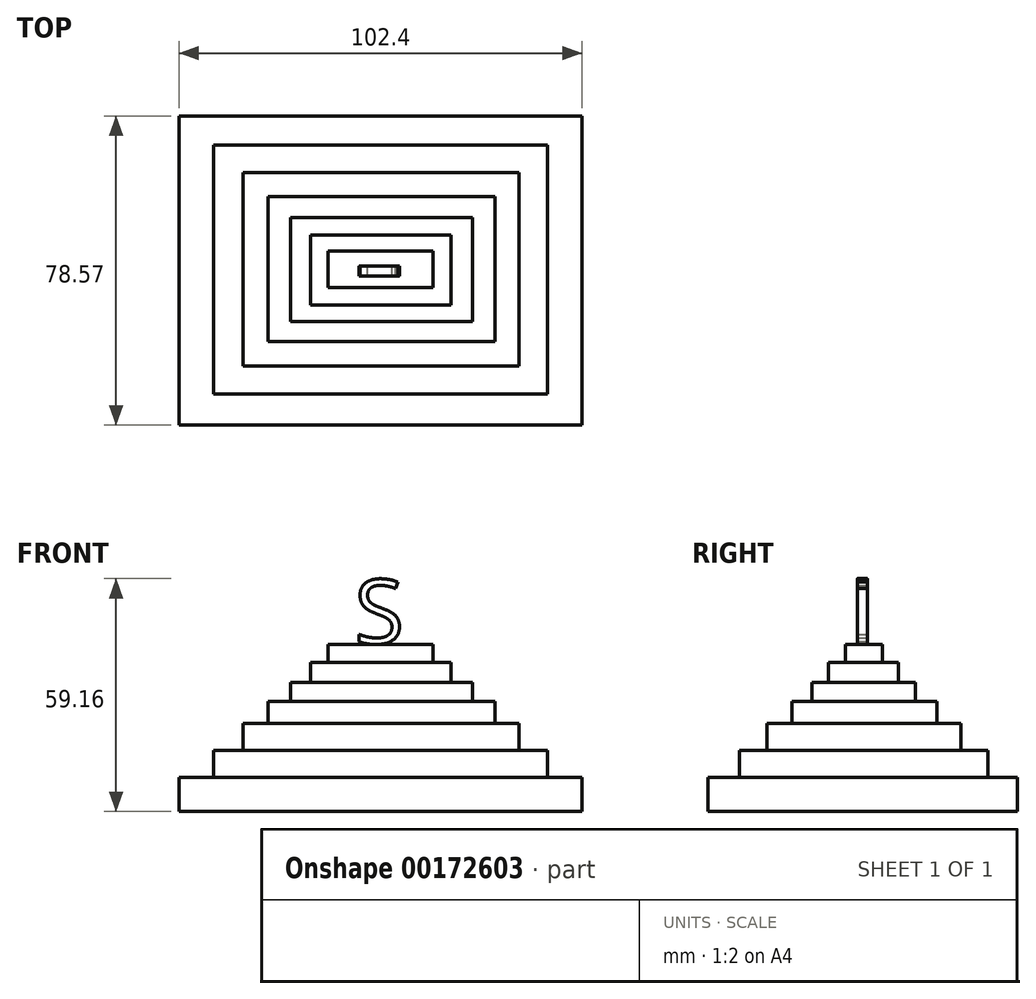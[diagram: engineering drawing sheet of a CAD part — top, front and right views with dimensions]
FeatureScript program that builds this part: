
annotation { "Feature Type Name" : "Feature", "Feature Type Description" : "" }
export const myFeature = defineFeature(function(context is Context, id is Id, definition is map)
    precondition{}
    {
        {
            var Q0;
            Q0=qCreatedBy(makeId("Top.planeOp"),FACE);
            var sketch = newSketch(context, id + "F0", { "sketchPlane" : qUnion([Q0])});
            skLineSegment(sketch, "E0.bottom", {"start": v(-50.86, 38.1) * mm, "end": v(51.54, 38.1) * mm});
            skLineSegment(sketch, "E0.top", {"start": v(-50.86, -40.47) * mm, "end": v(51.54, -40.47) * mm});
            skLineSegment(sketch, "E0.left", {"start": v(-50.86, 38.1) * mm, "end": v(-50.86, -40.47) * mm});
            skLineSegment(sketch, "E0.right", {"start": v(51.54, 38.1) * mm, "end": v(51.54, -40.47) * mm});
            skSolve(sketch);
        }
        {
            var Q0;
            Q0=qSketchRegion(id+"F0",true);
            var Q1;
            Q1=qSketchRegion(id+"FIFzSHws54il2H1_1",true);
            extrude(context, id + "F1", {"entities" : qUnion([Q0, Q1]), "depth" : 8.64 * mm});
        }
        {
            var Q0;
            Q0=qCreatedBy(makeId("Top.planeOp"),FACE);
            var sketch = newSketch(context, id + "F2", { "sketchPlane" : qUnion([Q0])});
            skLineSegment(sketch, "E1.bottom", {"start": v(-42.07, 30.67) * mm, "end": v(42.75, 30.67) * mm});
            skLineSegment(sketch, "E1.top", {"start": v(-42.07, -32.53) * mm, "end": v(42.75, -32.53) * mm});
            skLineSegment(sketch, "E1.left", {"start": v(-42.07, 30.67) * mm, "end": v(-42.07, -32.53) * mm});
            skLineSegment(sketch, "E1.right", {"start": v(42.75, 30.67) * mm, "end": v(42.75, -32.53) * mm});
            skSolve(sketch);
        }
        {
            var Q0;
            Q0=qSketchRegion(id+"F2",true);
            extrude(context, id + "F3", {"entities" : qUnion([Q0]), "operationType" : NewBodyOperationType.ADD, "depth" : 15.5 * mm});
        }
        {
            var Q0;
            Q0=qCreatedBy(makeId("Top.planeOp"),FACE);
            var sketch = newSketch(context, id + "F4", { "sketchPlane" : qUnion([Q0])});
            skLineSegment(sketch, "E2.bottom", {"start": v(-34.64, 23.74) * mm, "end": v(35.48, 23.74) * mm});
            skLineSegment(sketch, "E2.top", {"start": v(-34.64, -25.43) * mm, "end": v(35.48, -25.43) * mm});
            skLineSegment(sketch, "E2.left", {"start": v(-34.64, 23.74) * mm, "end": v(-34.64, -25.43) * mm});
            skLineSegment(sketch, "E2.right", {"start": v(35.48, 23.74) * mm, "end": v(35.48, -25.43) * mm});
            skSolve(sketch);
        }
        {
            var Q0;
            Q0=qSketchRegion(id+"F4",true);
            extrude(context, id + "F5", {"entities" : qUnion([Q0]), "operationType" : NewBodyOperationType.ADD, "depth" : 22.35 * mm});
        }
        {
            var Q0;
            Q0=qCreatedBy(makeId("Top.planeOp"),FACE);
            var sketch = newSketch(context, id + "F6", { "sketchPlane" : qUnion([Q0])});
            skLineSegment(sketch, "E3.bottom", {"start": v(-28.22, 17.66) * mm, "end": v(29.4, 17.66) * mm});
            skLineSegment(sketch, "E3.top", {"start": v(-28.22, -19.18) * mm, "end": v(29.4, -19.18) * mm});
            skLineSegment(sketch, "E3.left", {"start": v(-28.22, 17.66) * mm, "end": v(-28.22, -19.18) * mm});
            skLineSegment(sketch, "E3.right", {"start": v(29.4, 17.66) * mm, "end": v(29.4, -19.18) * mm});
            skSolve(sketch);
        }
        {
            var Q0;
            Q0=qSketchRegion(id+"F6",true);
            extrude(context, id + "F7", {"entities" : qUnion([Q0]), "operationType" : NewBodyOperationType.ADD, "depth" : 27.94 * mm});
        }
        {
            var Q0;
            Q0=qCreatedBy(makeId("Top.planeOp"),FACE);
            var sketch = newSketch(context, id + "F8", { "sketchPlane" : qUnion([Q0])});
            skLineSegment(sketch, "E4.bottom", {"start": v(-22.47, 12.25) * mm, "end": v(23.66, 12.25) * mm});
            skLineSegment(sketch, "E4.top", {"start": v(-22.47, -14.1) * mm, "end": v(23.66, -14.1) * mm});
            skLineSegment(sketch, "E4.left", {"start": v(-22.47, 12.25) * mm, "end": v(-22.47, -14.1) * mm});
            skLineSegment(sketch, "E4.right", {"start": v(23.66, 12.25) * mm, "end": v(23.66, -14.1) * mm});
            skSolve(sketch);
        }
        {
            var Q0;
            Q0=qSketchRegion(id+"F8",true);
            extrude(context, id + "F9", {"entities" : qUnion([Q0]), "operationType" : NewBodyOperationType.ADD, "depth" : 32.77 * mm});
        }
        {
            var Q0;
            Q0=qCreatedBy(makeId("Top.planeOp"),FACE);
            var sketch = newSketch(context, id + "F10", { "sketchPlane" : qUnion([Q0])});
            skLineSegment(sketch, "E5.bottom", {"start": v(-17.4, 7.86) * mm, "end": v(18.25, 7.86) * mm});
            skLineSegment(sketch, "E5.top", {"start": v(-17.4, -9.89) * mm, "end": v(18.25, -9.89) * mm});
            skLineSegment(sketch, "E5.left", {"start": v(-17.4, 7.86) * mm, "end": v(-17.4, -9.89) * mm});
            skLineSegment(sketch, "E5.right", {"start": v(18.25, 7.86) * mm, "end": v(18.25, -9.89) * mm});
            skSolve(sketch);
        }
        {
            var Q0;
            Q0=qSketchRegion(id+"F10",true);
            extrude(context, id + "F11", {"entities" : qUnion([Q0]), "operationType" : NewBodyOperationType.ADD, "depth" : 37.85 * mm});
        }
        {
            var Q0;
            Q0=qCreatedBy(makeId("Top.planeOp"),FACE);
            var sketch = newSketch(context, id + "F12", { "sketchPlane" : qUnion([Q0])});
            skLineSegment(sketch, "E6.bottom", {"start": v(-13.01, 3.8) * mm, "end": v(13.69, 3.8) * mm});
            skLineSegment(sketch, "E6.top", {"start": v(-13.01, -5.5) * mm, "end": v(13.69, -5.5) * mm});
            skLineSegment(sketch, "E6.left", {"start": v(-13.01, 3.8) * mm, "end": v(-13.01, -5.5) * mm});
            skLineSegment(sketch, "E6.right", {"start": v(13.69, 3.8) * mm, "end": v(13.69, -5.5) * mm});
            skSolve(sketch);
        }
        {
            var Q0;
            Q0=qSketchRegion(id+"F12",true);
            extrude(context, id + "F13", {"entities" : qUnion([Q0]), "operationType" : NewBodyOperationType.ADD, "depth" : 42.42 * mm});
        }
        {
            var Q0;
            Q0=qCreatedBy(makeId("Front.planeOp"),FACE);
            var sketch = newSketch(context, id + "F14", { "sketchPlane" : qUnion([Q0])});
            skArc(sketch, "E7", {"start": v(7.77, 42.5) * mm, "mid": v(0, 59.5) * mm, "end": v(-7.77, 42.5) * mm});
            skSolve(sketch);
        }
        {
            var Q0;
            Q0=qSketchRegion(id+"F14",true);
            var Q1;
            Q1=sQuery(id+"F14.wireOp",EDGE,"E7");
            extrude(context, id + "F15", {"entities" : qUnion([Q0]), "bodyType" : ToolBodyType.SURFACE, "surfaceEntities" : qUnion([Q1]), "depth" : 3.3 * mm});
        }
        {
            var Q0;
            Q0=qSketchRegion(id+"F14",true);
            var Q1;
            Q1=qConstructionFilter(qBodyType(qCreatedBy(id+"F14",EDGE),BodyType.WIRE),ConstructionObject.NO);
            extrude(context, id + "F16", {"entities" : qUnion([Q0]), "bodyType" : ToolBodyType.SURFACE, "surfaceEntities" : qUnion([Q1]), "oppositeDirection" : true, "depth" : 1.52 * mm});
        }
        {
            var Q0;
            Q0=qCreatedBy(makeId("Front.planeOp"),FACE);
            var sketch = newSketch(context, id + "F17", { "sketchPlane" : qUnion([Q0])});
            skText(sketch, "E8", { "text": "S", "fontName": "OpenSans-Regular.ttf"});
            const initialGuessF17  = {"E8": [-0.00625, 0.04267, 1, 0, 0.0164]};
            skSetInitialGuess(sketch, initialGuessF17);
            skSolve(sketch);
        }
        {
            var Q0;
            Q0=qSketchRegion(id+"F17",true);
            extrude(context, id + "F18", {"entities" : qUnion([Q0]), "depth" : 2.54 * mm});
        }
    });
